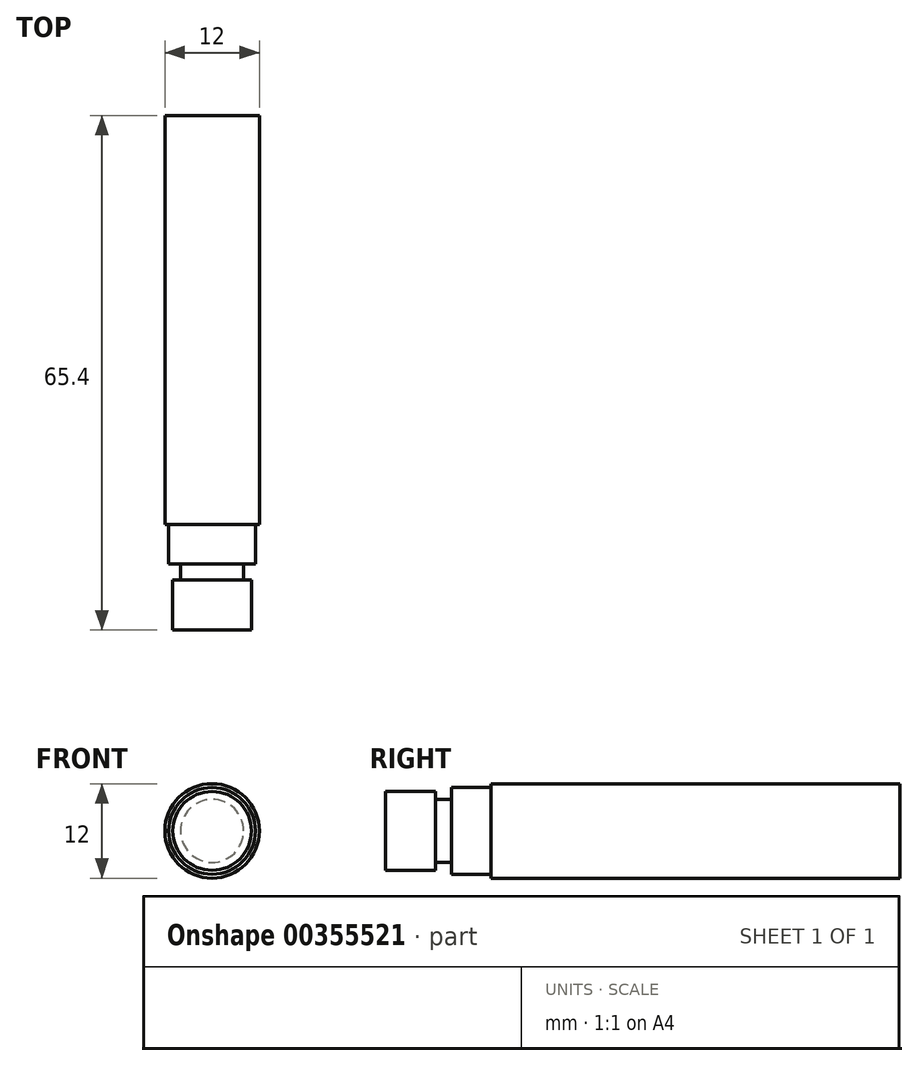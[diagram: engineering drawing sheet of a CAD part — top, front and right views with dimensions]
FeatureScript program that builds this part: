
annotation { "Feature Type Name" : "Feature", "Feature Type Description" : "" }
export const myFeature = defineFeature(function(context is Context, id is Id, definition is map)
    precondition{}
    {
        {
            var Q0;
            Q0=qCreatedBy(makeId("Front.planeOp"),FACE);
            var sketch = newSketch(context, id + "F0", { "sketchPlane" : qUnion([Q0])});
            skCircle(sketch, "E0", {"center": v(0, 0) * mm, "radius": 6 * mm});
            skSolve(sketch);
        }
        {
            var Q0;
            Q0 = qSketchRegion(id + "F0", true);
            extrude(context, id + "F1", {"entities" : qUnion([Q0]), "oppositeDirection" : true, "depth" : 52 * mm});
        }
        {
            var Q0;
            Q0=makeQuery(id+"F1.opExtrude","CAP_FACE",FACE,{"disambiguationData":[OSD([sQuery(id+"F0.wireOp",EDGE,"E0")])],"isStart":true});
            var sketch = newSketch(context, id + "F2", { "sketchPlane" : qUnion([Q0])});
            skCircle(sketch, "E1", {"center": v(0, 0) * mm, "radius": 5.5 * mm});
            skSolve(sketch);
        }
        {
            var Q0;
            Q0 = qSketchRegion(id + "F2", true);
            extrude(context, id + "F3", {"entities" : qUnion([Q0]), "operationType" : NewBodyOperationType.ADD, "depth" : 5 * mm});
        }
        {
            var Q0;
            Q0=makeQuery(id+"F3.opExtrude","CAP_FACE",FACE,{"disambiguationData":[OSD([sQuery(id+"F2.wireOp",EDGE,"E1")])],"isStart":false});
            var sketch = newSketch(context, id + "F4", { "sketchPlane" : qUnion([Q0])});
            skCircle(sketch, "E2", {"center": v(0, 0) * mm, "radius": 4 * mm});
            skSolve(sketch);
        }
        {
            var Q0;
            Q0=makeQuery(id+"F4.imprint","IMPRINT",FACE,{"disambiguationData":[TD([[makeQuery(id+"F4.imprint","IMPRINT",EDGE,{"derivedFrom":sQuery(id+"F4.wireOp",EDGE,"E2")}),1.0]])]});
            extrude(context, id + "F5", {"entities" : qUnion([Q0]), "operationType" : NewBodyOperationType.ADD, "depth" : 2 * mm});
        }
        {
            var Q0;
            Q0=makeQuery(id+"F5.opExtrude","CAP_FACE",FACE,{"disambiguationData":[OSD([sQuery(id+"F4.wireOp",EDGE,"E2")])],"isStart":false});
            var sketch = newSketch(context, id + "F6", { "sketchPlane" : qUnion([Q0])});
            skCircle(sketch, "E3", {"center": v(0, 0) * mm, "radius": 5 * mm});
            skSolve(sketch);
        }
        {
            var Q0;
            Q0 = qSketchRegion(id + "F6", true);
            extrude(context, id + "F7", {"entities" : qUnion([Q0]), "operationType" : NewBodyOperationType.ADD, "depth" : 6.4 * mm});
        }
    });
